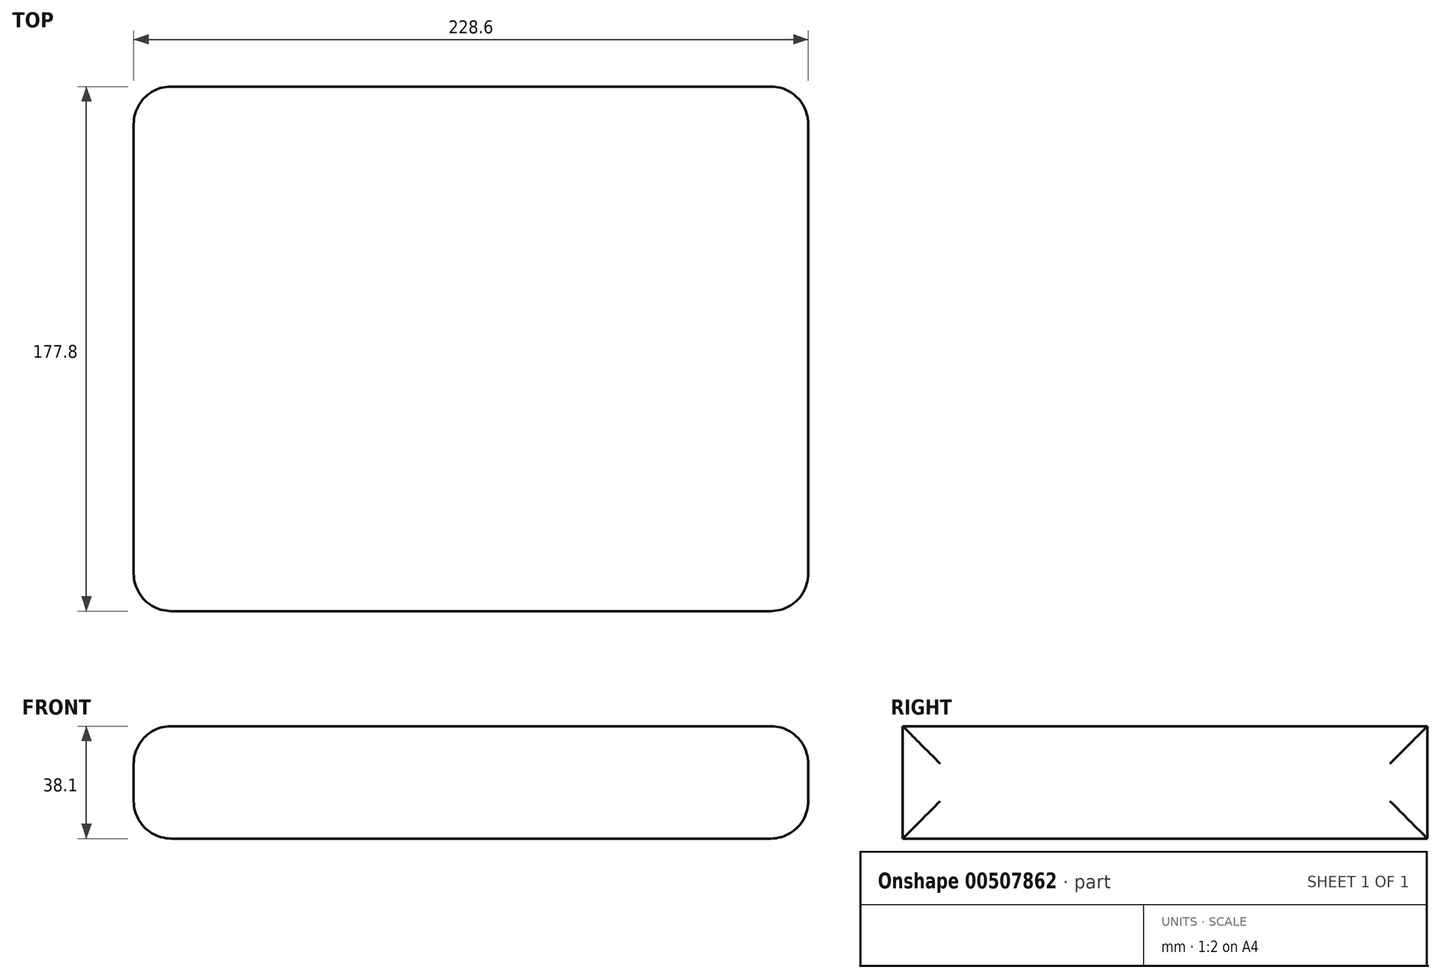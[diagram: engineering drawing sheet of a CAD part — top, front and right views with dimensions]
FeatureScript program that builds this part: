
annotation { "Feature Type Name" : "Feature", "Feature Type Description" : "" }
export const myFeature = defineFeature(function(context is Context, id is Id, definition is map)
    precondition{}
    {
        {
            var Q0;
            Q0=qCreatedBy(makeId("Top.planeOp"),FACE);
            var sketch = newSketch(context, id + "F0", { "sketchPlane" : qUnion([Q0])});
            skLineSegment(sketch, "E0.bottom", {"start": v(-114.3, 88.9) * mm, "end": v(114.3, 88.9) * mm});
            skLineSegment(sketch, "E0.top", {"start": v(-114.3, -88.9) * mm, "end": v(114.3, -88.9) * mm});
            skLineSegment(sketch, "E0.left", {"start": v(-114.3, 88.9) * mm, "end": v(-114.3, -88.9) * mm});
            skLineSegment(sketch, "E0.right", {"start": v(114.3, 88.9) * mm, "end": v(114.3, -88.9) * mm});
            skPoint(sketch, "E0.middle", {"position": v(0, 0) * mm});
            skSolve(sketch);
        }
        {
            var Q0;
            Q0 = qSketchRegion(id + "F0", true);
            extrude(context, id + "F1", {"entities" : qUnion([Q0]), "depth" : 38.1 * mm, "offsetDistance" : 25.4 * mm});
        }
        {
            var Q0;
            Q0=makeQuery(id+"F1.opExtrude","SWEPT_FACE",FACE,{"disambiguationData":[OSD([sQuery(id+"F0.wireOp",EDGE,"E0.left")])]});
            var Q1;
            Q1=makeQuery(id+"F1.opExtrude","SWEPT_FACE",FACE,{"disambiguationData":[OSD([sQuery(id+"F0.wireOp",EDGE,"E0.right")])]});
            fillet(context, id + "F2", {"entities" : qUnion([Q0, Q1]), "radius" : 12.7 * mm, "tangentPropagation" : true, "allowEdgeOverflow" : false});
        }
    });
